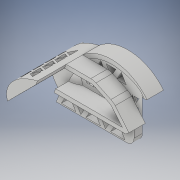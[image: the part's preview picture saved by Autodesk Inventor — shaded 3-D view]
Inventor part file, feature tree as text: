
AUTODESK INVENTOR PART (.ipt)
format: ipt  version: 2017 (Build 210142000, 142)  size: 1,078,784 bytes
history: native  units: mm
features: sketch x32, extrude x28, plane x9, fillet x4, other x3, revolve x1, boolean_combine x1
ambient origin geometry x8: Origin, YZ Plane, XZ Plane, XY Plane, X Axis, Y Axis, Z Axis, Center Point
bodies: Solid1 (feature_tree), Solid2 (feature_tree)
feature tree (78):
  extrude  "Extrusion1"  Depth=35.0mm
  plane  "Work Plane1"
  extrude  "Extrusion2"  Depth=33.005006mm
  other  "Bend Part1"
  other  "Bend Part2"
  extrude  "Extrusion3"  Depth=32.454mm
  plane  "Work Plane2"
  extrude  "Extrusion4"  Depth=20.0mm
  other  "Bend Part3"
  extrude  "Extrusion5"  Depth=30.0mm
  revolve  "Revolution1"  [1 undecoded]
  plane  "Work Plane3"
  extrude  "Extrusion6"  Depth=10.0mm
  boolean_combine  "Combine1"
  plane  "Work Plane4"
  extrude  "Extrusion7"  TaperAngle=90.0deg  [1 undecoded]
  extrude  "Extrusion8"  Depth=80.0mm
  extrude  "Extrusion9"  Depth=50.0mm TaperAngle=135.0deg
  extrude  "Extrusion10"  Depth=35.0mm
  plane  "Work Plane5"
  extrude  "Extrusion11"  Depth=60.0mm
  extrude  "Extrusion12"  Depth=60.0mm
  plane  "Work Plane6"
  extrude  "Extrusion13"  [1 undecoded]
  extrude  "Extrusion14"  Depth=30.0mm TaperAngle=0.0deg
  plane  "Work Plane7"
  extrude  "Extrusion15"  Depth=20.0mm TaperAngle=0.0deg
  extrude  "Extrusion16"  Depth=15.219936mm
  extrude  "Extrusion17"  Depth=15.155142mm
  fillet  "Fillet1"  Radius=20.0mm
  extrude  "Extrusion18"  Depth=100.334153mm
  fillet  "Fillet2"  Radius=43.193283mm
  fillet  "Fillet3"  Radius=60.0mm
  fillet  "Fillet4"  Radius=60.5mm
  extrude  "Extrusion19"  Depth=25.287025mm
  extrude  "Extrusion20"  Depth=2.439mm TaperAngle=0.0deg
  extrude  "Extrusion21"  Depth=0.980484mm
  extrude  "Extrusion22"  Depth=2.246206mm
  extrude  "Extrusion23"  Depth=100.0mm TaperAngle=0.0deg
  extrude  "Extrusion24"  Depth=5.0mm TaperAngle=0.0deg
  extrude  "Extrusion25"  Depth=95.197mm TaperAngle=0.0deg
  extrude  "Extrusion26"  Depth=60.0mm
  extrude  "Extrusion27"  Depth=20.0mm
  plane  "Work Plane9"
  extrude  "Extrusion28"  Depth=116.447mm TaperAngle=0.0deg
  sketch  "Sketch1"  dims[d0=60.0mm d1=35.0mm]
  sketch  "Sketch2"  dims[d2=60.0mm d3=33.005006mm]
  sketch  "Sketch3"  dims[d4=75.0mm d5=0.0mm d6=32.454mm]
  sketch  "Sketch4"  dims[d7=85.0mm d8=20.0mm]
  sketch  "Sketch5"  dims[d9=5.0mm d10=0.0mm d11=30.0mm]
  sketch  "Sketch6"  dims[d12=55.0mm d13=10.0mm d14=4.363323mm]
  sketch  "Sketch7"  dims[d15=20.0mm d16=10.0mm d17=4.363323mm]
  sketch  "Sketch8"  dims[d18=20.0mm d19=0.0mm d20=90.0deg]
  sketch  "Sketch9"  dims[d21=20.0mm d22=80.0mm]
  sketch  "Sketch10"  dims[d23=5.0mm d24=0.0mm d25=50.0mm d26=135.0deg]
  sketch  "Sketch11"  dims[d27=60.0mm d28=35.0mm]
  sketch  "Sketch12"  dims[d29=35.0mm d30=60.0mm]
  sketch  "Sketch13"  dims[d31=20.0mm d32=0.0mm d33=60.0mm]
  sketch  "Sketch14"  dims[d34=270.0deg d35=-4.697mm]
  sketch  "Sketch15"  dims[d36=20.0mm d37=30.0mm d38=0.0mm]
  sketch  "Sketch16"  dims[d39=-20.0mm d40=20.0mm d41=0.0mm]
  sketch  "Sketch17"  dims[d42=35.67mm d43=15.219936mm]
  sketch  "Sketch18"  dims[d44=35.67mm d45=15.155142mm d46=20.0mm d47=0.0mm]
  sketch  "Sketch19"  dims[d48=20.0mm d49=0.0mm d50=100.334153mm d51=43.193283mm d52=60.0mm d53=0.0mm d54=60.5mm]
  sketch  "Sketch20"  dims[d55=14.497104mm d56=25.287025mm]
  sketch  "Sketch21"  dims[d57=104.0mm d58=0.0mm d59=2.439mm d60=0.0mm]
  sketch  "Sketch22"  dims[d61=-31.25mm d62=0.980484mm]
  sketch  "Sketch23"  dims[d63=1.164325mm d64=2.246206mm]
  sketch  "Sketch24"  dims[d65=25.536883mm d66=100.0mm d67=0.0mm]
  sketch  "Sketch25"  dims[d68=0.0mm d69=5.0mm d70=0.0mm]
  sketch  "Sketch26"  dims[d71=50.209mm d72=95.197mm d73=0.0mm]
  sketch  "Sketch27"  dims[d74=95.197mm d75=0.0mm d76=60.0mm]
  sketch  "Sketch28"  dims[d77=60.0mm d78=20.0mm]
  sketch  "Sketch29"  dims[d79=18.461mm d80=116.447mm d81=0.0mm]
  sketch  "Sketch30"  dims[d82=10.0mm]
  sketch  "Sketch31"  dims[d83=8.797686mm]
  plane  "Work Plane8"
  sketch  "Sketch32"  dims[d84=116.447mm d85=0.0mm d86=10.0mm d87=9.0mm d88=10.0mm d89=60.197145mm d90=34.482005mm d91=20.0mm d92=3.0mm d93=20.0mm d94=90.0deg d95=55.512917mm d96=23.386841mm d97=11.976391mm d98=75.0mm d99=0.0mm d100=3.0mm d101=20.0mm d102=75.0mm d103=0.0mm d104=14.0mm d105=2.0mm d106=75.0mm d107=0.0mm d108=65.72713mm d109=31.278947mm d110=8.340283mm d111=36.051467mm d112=20.0mm d113=0.0mm d114=10.0mm d115=18.461203mm d116=94.75mm d117=0.0mm d118=1.594016mm d119=1.594016mm d120=11.43616mm d121=30.0mm d123=30.0mm d124=10.0mm d126=10.0mm d128=15.0mm d129=1.594016mm d130=20.0mm d132=30.0mm d133=10.0mm d135=10.0mm d137=10.0mm d138=0.0mm d139=10.0mm d140=5.0mm d141=5.0mm d142=150.0deg d143=30.0mm d145=15.0mm d146=20.0mm d148=15.0mm d151=7.5mm d152=13.66mm d153=30.0mm d155=15.0mm d156=10.0mm d158=10.0mm d160=30.0mm d162=15.0mm d163=10.0mm d165=10.0mm d167=100.0mm d168=0.0mm d169=2.0mm d170=11.794865mm d171=5.404884mm d172=24.334275mm d173=20.0mm d175=25.0mm d176=10.0mm d178=10.0mm d180=2.0mm d181=12.5mm d182=31.25mm d183=0.0mm d184=4.0mm d185=5.334176mm d186=38.18999mm d187=70.0mm d189=10.0mm d190=40.0mm d192=10.0mm d195=38.503494mm d196=5.0mm d197=60.0mm d199=10.0mm d200=40.0mm d202=10.0mm d205=31.25mm d206=0.0mm d207=21.0mm d208=6.214mm d209=3.0mm d210=0.0mm d211=70.0mm d213=10.0mm d214=30.0mm d216=10.0mm d219=5.0mm d220=3.0mm d221=60.0mm d223=10.0mm d224=30.0mm d226=10.0mm d229=9.75mm d230=0.0mm]
note: 3 required parameter values undecoded (feature->parameter linkage not recoverable at this tier; creation-order binding heuristic only, values carry confidence <= 0.55)